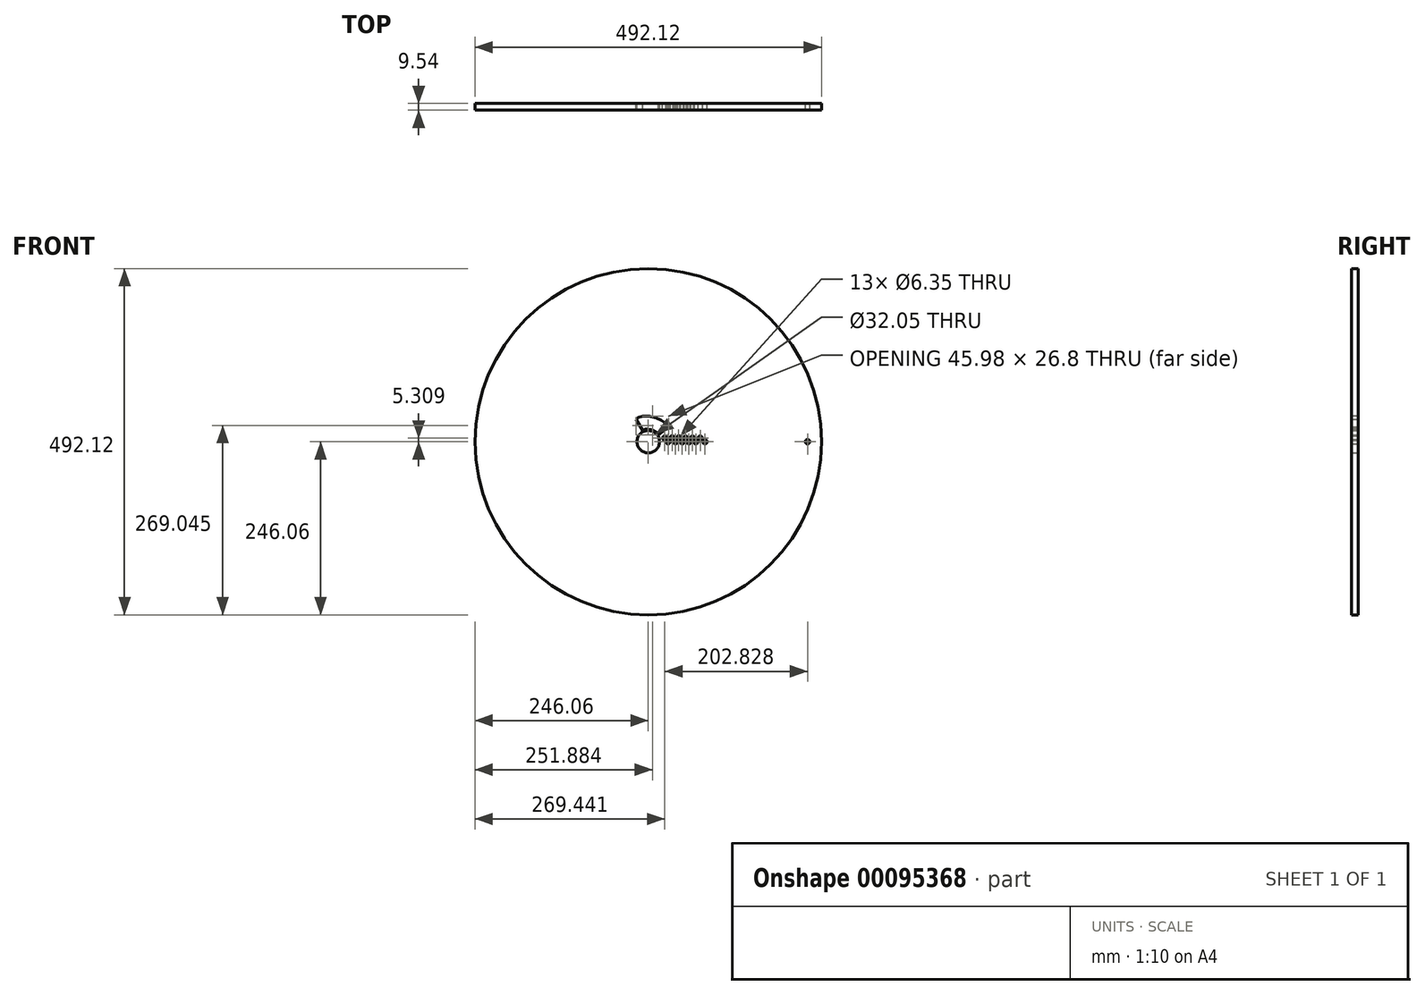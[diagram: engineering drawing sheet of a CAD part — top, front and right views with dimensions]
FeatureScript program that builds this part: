
annotation { "Feature Type Name" : "Feature", "Feature Type Description" : "" }
export const myFeature = defineFeature(function(context is Context, id is Id, definition is map)
    precondition{}
    {
        {
            var Q0;
            Q0=qCreatedBy(makeId("Front.planeOp"),FACE);
            var sketch = newSketch(context, id + "F0", { "sketchPlane" : qUnion([Q0])});
            skCircle(sketch, "E0", {"center": v(0, 0) * mm, "radius": 246.06 * mm});
            skCircle(sketch, "E1", {"center": v(0, 0) * mm, "radius": 16.02 * mm});
            skSolve(sketch);
        }
        {
            var Q0;
            Q0=makeQuery(id+"F0.imprint","IMPRINT",FACE,{"disambiguationData":[TD([[makeQuery(id+"F0.imprint","IMPRINT",EDGE,{"derivedFrom":sQuery(id+"F0.wireOp",EDGE,"E0")}),1.0]])]});
            extrude(context, id + "F1", {"entities" : qUnion([Q0]), "depth" : 4.76 * mm});
        }
        {
            var Q0;
            Q0=makeQuery(id+"F1.opExtrude","CAP_FACE",FACE,{"disambiguationData":[OSD([sQuery(id+"F0.wireOp",EDGE,"E0"),sQuery(id+"F0.wireOp",EDGE,"E1")])],"isStart":false});
            extrude(context, id + "F2", {"entities" : qUnion([Q0]), "operationType" : NewBodyOperationType.ADD, "depth" : 4.78 * mm});
        }
        {
            var Q0;
            Q0=qCreatedBy(makeId("Front.planeOp"),FACE);
            var sketch = newSketch(context, id + "F3", { "sketchPlane" : qUnion([Q0])});
            skPoint(sketch, "E2", {"position": v(28.04, 0) * mm});
            skPoint(sketch, "E3", {"position": v(38.51, 0) * mm});
            skPoint(sketch, "E4", {"position": v(48.12, 0) * mm});
            skPoint(sketch, "E5", {"position": v(57.72, 0) * mm});
            skPoint(sketch, "E6", {"position": v(67.61, 0) * mm});
            skPoint(sketch, "E7", {"position": v(33.86, 5.3) * mm});
            skPoint(sketch, "E8", {"position": v(43.17, 5.3) * mm});
            skPoint(sketch, "E9", {"position": v(53.06, 5.02) * mm});
            skPoint(sketch, "E10", {"position": v(62.66, 5.02) * mm});
            skPoint(sketch, "E11", {"position": v(73.72, 5.02) * mm});
            skPoint(sketch, "E12", {"position": v(80.42, 0) * mm});
            skPoint(sketch, "E13", {"position": v(23.38, 5.02) * mm});
            skSolve(sketch);
        }
        {
            var Q0;
            Q0=sQuery(id+"F3.wireOp",VERTEX,"E13");
            var Q1;
            Q1=sQuery(id+"F3.wireOp",VERTEX,"E2");
            var Q2;
            Q2=sQuery(id+"F3.wireOp",VERTEX,"E7");
            var Q3;
            Q3=sQuery(id+"F3.wireOp",VERTEX,"E3");
            var Q4;
            Q4=sQuery(id+"F3.wireOp",VERTEX,"E8");
            var Q5;
            Q5=sQuery(id+"F3.wireOp",VERTEX,"E4");
            var Q6;
            Q6=sQuery(id+"F3.wireOp",VERTEX,"E5");
            var Q7;
            Q7=sQuery(id+"F3.wireOp",VERTEX,"E10");
            var Q8;
            Q8=sQuery(id+"F3.wireOp",VERTEX,"E6");
            var Q9;
            Q9=sQuery(id+"F3.wireOp",VERTEX,"E11");
            var Q10;
            Q10=sQuery(id+"F3.wireOp",VERTEX,"E9");
            var Q11;
            Q11=sQuery(id+"F3.wireOp",VERTEX,"E12");
            var Q12;
            Q12=makeQuery(id+"F1.opExtrude","SWEPT_BODY",BODY,{"disambiguationData":[OSD([sQuery(id+"F0.wireOp",EDGE,"E0"),sQuery(id+"F0.wireOp",EDGE,"E1")])]});
            hole(context, id + "F4", {"style" : HoleStyle.SIMPLE, "endStyle" : HoleEndStyle.THROUGH, "oppositeDirection" : true, "holeDiameter" : 6.35 * mm, "locations" : qUnion([Q0, Q1, Q2, Q3, Q4, Q5, Q6, Q7, Q8, Q9, Q10, Q11]), "scope" : qUnion([Q12]), "isTappedThrough" : true});
        }
        {
            var Q0;
            Q0=qCreatedBy(makeId("Front.planeOp"),FACE);
            var sketch = newSketch(context, id + "F5", { "sketchPlane" : qUnion([Q0])});
            skLineSegment(sketch, "E14", {"start": v(14.46, 9.59) * mm, "end": v(28.82, 21.09) * mm});
            skFitSpline(sketch, "E15", {"points": [v(28.82, 21.09) * mm, v(-17.17, 31.92) * mm], "startDerivative": vector(-19.07, 34.26) * mm, "endDerivative": vector(-32.95, -32.36) * mm});
            skFitSpline(sketch, "E16", {"points": [v(14.46, 9.59) * mm, v(-8.14, 16.07) * mm], "startDerivative": vector(-5.17, 22.1) * mm, "endDerivative": vector(-11.1, -11.57) * mm});
            skLineSegment(sketch, "E17", {"start": v(-8.14, 16.07) * mm, "end": v(-17.17, 31.92) * mm});
            skSolve(sketch);
        }
        {
            var Q0;
            Q0=makeQuery(id+"F5.imprint","IMPRINT",FACE,{"disambiguationData":[TD([[makeQuery(id+"F5.imprint","IMPRINT",EDGE,{"derivedFrom":sQuery(id+"F5.wireOp",EDGE,"E14")}),1.0]])]});
            extrude(context, id + "F6", {"entities" : qUnion([Q0]), "operationType" : NewBodyOperationType.REMOVE, "endBound" : BoundingType.THROUGH_ALL, "depth" : 25.4 * mm});
        }
        {
            var Q0;
            Q0=qCreatedBy(makeId("Front.planeOp"),FACE);
            var sketch = newSketch(context, id + "F7", { "sketchPlane" : qUnion([Q0])});
            skCircle(sketch, "E18", {"center": v(226.2, 0) * mm, "radius": 4.76 * mm});
            skSolve(sketch);
        }
        {
            var Q0;
            Q0=sQuery(id+"F7.wireOp",VERTEX,"E18.center");
            var Q1;
            Q1=makeQuery(id+"F1.opExtrude","SWEPT_BODY",BODY,{"disambiguationData":[OSD([sQuery(id+"F0.wireOp",EDGE,"E0"),sQuery(id+"F0.wireOp",EDGE,"E1")])]});
            hole(context, id + "F8", {"style" : HoleStyle.SIMPLE, "endStyle" : HoleEndStyle.THROUGH, "oppositeDirection" : true, "holeDiameter" : 6.35 * mm, "locations" : qUnion([Q0]), "scope" : qUnion([Q1]), "isTappedThrough" : true});
        }
    });
